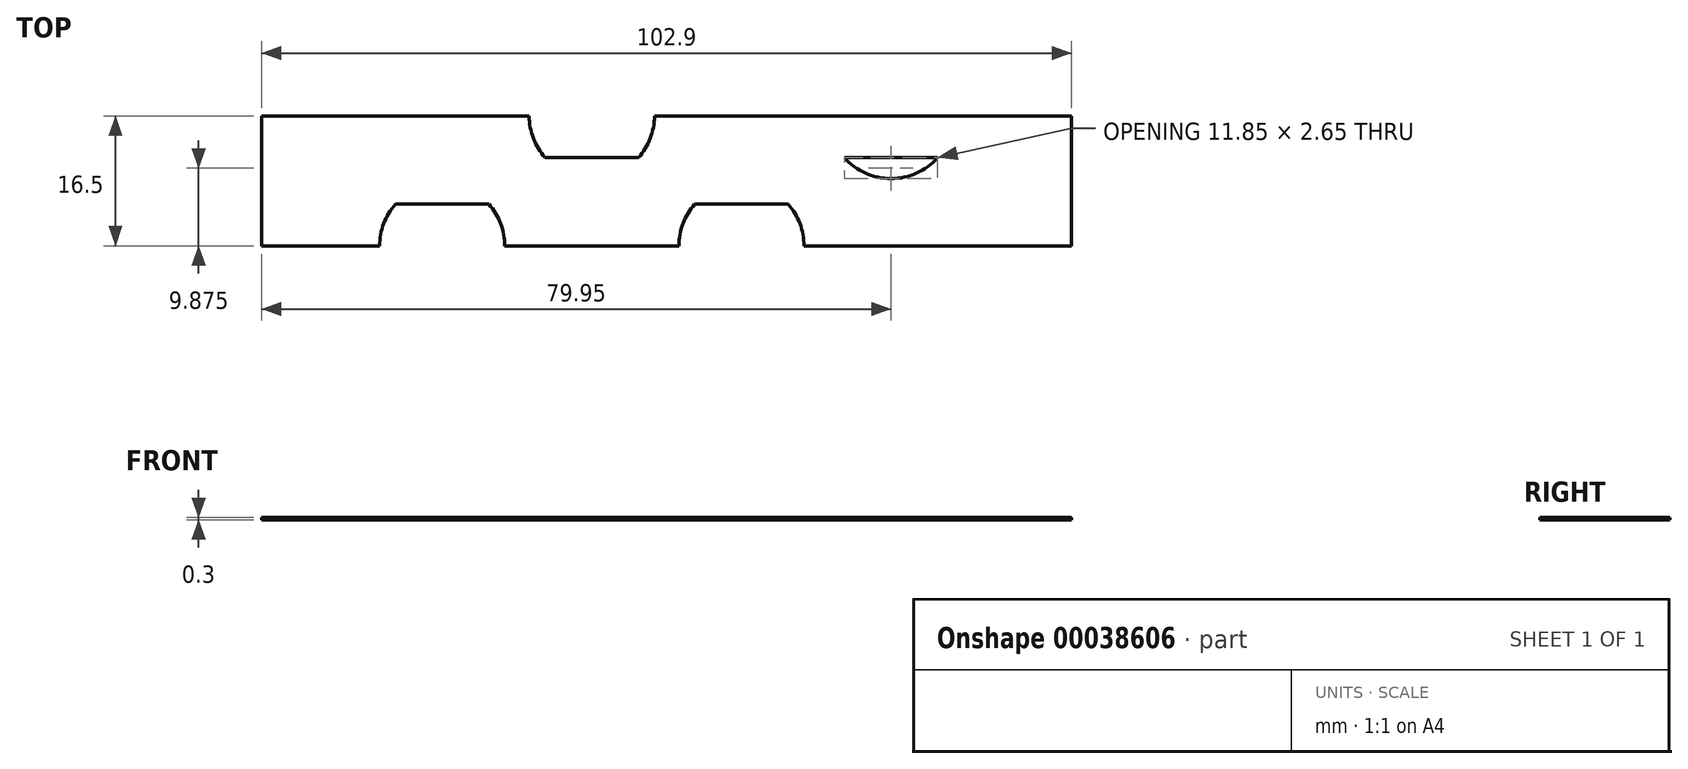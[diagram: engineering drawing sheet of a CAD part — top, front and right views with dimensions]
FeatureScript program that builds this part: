
annotation { "Feature Type Name" : "Feature", "Feature Type Description" : "" }
export const myFeature = defineFeature(function(context is Context, id is Id, definition is map)
    precondition{}
    {
        {
            var Q0;
            Q0=qCreatedBy(makeId("Top.planeOp"),FACE);
            var sketch = newSketch(context, id + "F0", { "sketchPlane" : qUnion([Q0])});
            skLineSegment(sketch, "E0.bottom", {"start": v(0, -8.25) * mm, "end": v(102.9, -8.25) * mm});
            skLineSegment(sketch, "E0.top", {"start": v(0, 8.25) * mm, "end": v(102.9, 8.25) * mm});
            skLineSegment(sketch, "E0.left", {"start": v(0, -8.25) * mm, "end": v(0, 8.25) * mm});
            skLineSegment(sketch, "E0.right", {"start": v(102.9, -8.25) * mm, "end": v(102.9, 8.25) * mm});
            skCircle(sketch, "E1", {"center": v(22.95, -8.25) * mm, "radius": 7.95 * mm});
            skCircle(sketch, "E2", {"center": v(41.95, 8.25) * mm, "radius": 7.95 * mm});
            skCircle(sketch, "E3", {"center": v(60.95, -8.25) * mm, "radius": 7.95 * mm});
            skCircle(sketch, "E4", {"center": v(79.95, 8.25) * mm, "radius": 7.95 * mm});
            skLineSegment(sketch, "E5", {"start": v(17.02, -2.95) * mm, "end": v(28.88, -2.95) * mm});
            skLineSegment(sketch, "E6", {"start": v(36.02, 2.95) * mm, "end": v(47.88, 2.95) * mm});
            skLineSegment(sketch, "E7", {"start": v(55.02, -2.95) * mm, "end": v(66.88, -2.95) * mm});
            skLineSegment(sketch, "E8", {"start": v(73.72, 2.95) * mm, "end": v(85.88, 2.95) * mm});
            skSolve(sketch);
        }
        {
            var Q0;
            {var subQ5=sQuery(id+"F0.wireOp",EDGE,"E0.left");Q0=makeQuery(id+"F0.imprint","IMPRINT",FACE,{"disambiguationData":[TD([[makeQuery(id+"F0.imprint","IMPRINT",EDGE,{"derivedFrom":subQ5}),-1.0]])]});}
            var Q1;
            {var subQ0=sQuery(id+"F0.wireOp",EDGE,"E5");Q1=makeQuery(id+"F0.imprint","IMPRINT",FACE,{"disambiguationData":[TD([[makeQuery(id+"F0.imprint","IMPRINT",EDGE,{"derivedFrom":subQ0}),1.0]])]});}
            var Q2;
            {var subQ0=sQuery(id+"F0.wireOp",EDGE,"E6");Q2=makeQuery(id+"F0.imprint","IMPRINT",FACE,{"disambiguationData":[TD([[makeQuery(id+"F0.imprint","IMPRINT",EDGE,{"derivedFrom":subQ0}),-1.0]])]});}
            var Q3;
            {var subQ0=sQuery(id+"F0.wireOp",EDGE,"E7");Q3=makeQuery(id+"F0.imprint","IMPRINT",FACE,{"disambiguationData":[TD([[makeQuery(id+"F0.imprint","IMPRINT",EDGE,{"derivedFrom":subQ0}),1.0]])]});}
            var Q4;
            {var subQ0=sQuery(id+"F0.wireOp",EDGE,"E8");var subQ1=sQuery(id+"F0.wireOp",EDGE,"E4");var subQ2=makeQuery(id+"F0.imprint","INTERSECT",VERTEX,{"disambiguationData":[OD(0.0)],"derivedFrom":[subQ1,subQ0]});Q4=makeQuery(id+"F0.imprint","IMPRINT",FACE,{"disambiguationData":[TD([[makeQuery(id+"F0.imprint","IMPRINT",EDGE,{"disambiguationData":[TD([[subQ2,1.0]])],"derivedFrom":subQ1}),1.0]])]});}
            extrude(context, id + "F1", {"entities" : qUnion([Q0, Q1, Q2, Q3, Q4]), "depth" : 0.3 * mm});
        }
    });
